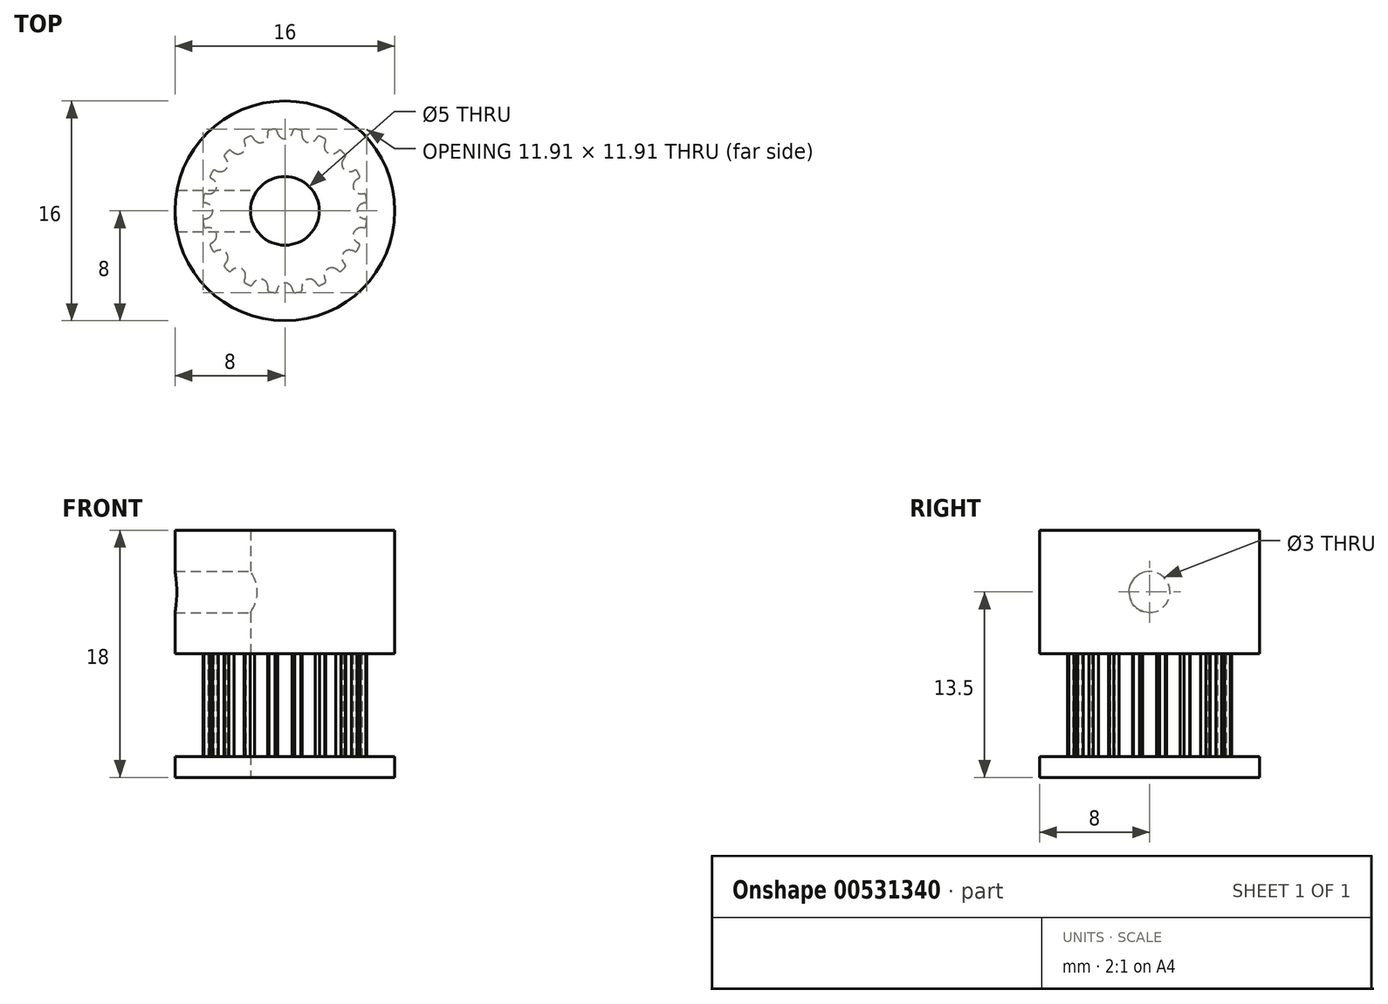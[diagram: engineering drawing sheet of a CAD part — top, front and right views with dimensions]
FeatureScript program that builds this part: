
annotation { "Feature Type Name" : "Feature", "Feature Type Description" : "" }
export const myFeature = defineFeature(function(context is Context, id is Id, definition is map)
    precondition{}
    {
        {
            var Q0;
            Q0=qCreatedBy(makeId("Top.planeOp"),FACE);
            var sketch = newSketch(context, id + "F0", { "sketchPlane" : qUnion([Q0])});
            skLineSegment(sketch, "E0", {"start": v(-19.17, 17.78) * mm, "end": v(-18.17, 17.78) * mm});
            skLineSegment(sketch, "E1", {"start": v(-18.17, 17.78) * mm, "end": v(-18.17, 18.4) * mm});
            skArc(sketch, "E2", {"start": v(-18.67, 18.85) * mm, "mid": v(-18.88, 19.07) * mm, "end": v(-19.17, 19.16) * mm});
            skArc(sketch, "E3", {"start": v(-18.58, 18.54) * mm, "mid": v(-18.61, 18.7) * mm, "end": v(-18.67, 18.85) * mm});
            skArc(sketch, "E4", {"start": v(-18.58, 18.54) * mm, "mid": v(-18.53, 18.44) * mm, "end": v(-18.43, 18.4) * mm});
            skLineSegment(sketch, "E5", {"start": v(-18.43, 18.4) * mm, "end": v(-18.17, 18.4) * mm});
            skArc(sketch, "E6.0.MirrorCS", {"start": v(-19.67, 18.85) * mm, "mid": v(-19.47, 19.07) * mm, "end": v(-19.17, 19.16) * mm});
            skArc(sketch, "E7.0.MirrorCS", {"start": v(-19.76, 18.54) * mm, "mid": v(-19.73, 18.7) * mm, "end": v(-19.67, 18.85) * mm});
            skArc(sketch, "E8.0.MirrorCS", {"start": v(-19.76, 18.54) * mm, "mid": v(-19.81, 18.44) * mm, "end": v(-19.91, 18.4) * mm});
            skLineSegment(sketch, "E9.0.MirrorCS", {"start": v(-19.91, 18.4) * mm, "end": v(-20.17, 18.4) * mm});
            skLineSegment(sketch, "E10.0.MirrorCS", {"start": v(-20.17, 17.78) * mm, "end": v(-20.17, 18.4) * mm});
            skLineSegment(sketch, "E11.0.MirrorCS", {"start": v(-19.17, 17.78) * mm, "end": v(-20.17, 17.78) * mm});
            skLineSegment(sketch, "E12.direction1", {"start": v(-20.17, 17.78) * mm, "end": v(-18.17, 17.78) * mm, "construction": true});
            skLineSegment(sketch, "E13", {"start": v(-20.17, 18.15) * mm, "end": v(-18.17, 18.15) * mm, "construction": true});
            skPoint(sketch, "E14", {"position": v(0, -5.25) * mm});
            skArc(sketch, "E15", {"start": v(0.51, -5.6) * mm, "mid": v(0, -5.25) * mm, "end": v(-0.51, -5.6) * mm});
            skArc(sketch, "E16", {"start": v(-0.51, -5.6) * mm, "mid": v(-0.56, -5.71) * mm, "end": v(-0.59, -5.83) * mm});
            skArc(sketch, "E17", {"start": v(0.59, -5.83) * mm, "mid": v(0.56, -5.71) * mm, "end": v(0.51, -5.6) * mm});
            skArc(sketch, "E18", {"start": v(0.72, -5.96) * mm, "mid": v(0.94, -5.93) * mm, "end": v(1.16, -5.89) * mm});
            skArc(sketch, "E19", {"start": v(0.59, -5.83) * mm, "mid": v(0.66, -5.94) * mm, "end": v(0.8, -5.95) * mm});
            skArc(sketch, "E20", {"start": v(-0.59, -5.83) * mm, "mid": v(-0.66, -5.94) * mm, "end": v(-0.8, -5.95) * mm});
            skArc(sketch, "E21.1.0", {"start": v(2.22, -5.16) * mm, "mid": v(1.62, -5) * mm, "end": v(1.24, -5.48) * mm});
            skPoint(sketch, "E21.1.1", {"position": v(1.62, -5) * mm});
            skArc(sketch, "E21.1.2", {"start": v(1.24, -5.48) * mm, "mid": v(1.23, -5.6) * mm, "end": v(1.24, -5.73) * mm});
            skArc(sketch, "E21.1.3", {"start": v(2.36, -5.37) * mm, "mid": v(2.47, -5.44) * mm, "end": v(2.6, -5.41) * mm});
            skArc(sketch, "E21.1.4", {"start": v(1.24, -5.73) * mm, "mid": v(1.2, -5.85) * mm, "end": v(1.08, -5.9) * mm});
            skArc(sketch, "E21.1.5", {"start": v(2.36, -5.37) * mm, "mid": v(2.3, -5.26) * mm, "end": v(2.22, -5.16) * mm});
            skArc(sketch, "E22.3.2.0", {"start": v(3.7, -4.22) * mm, "mid": v(3.09, -4.25) * mm, "end": v(2.87, -4.83) * mm});
            skPoint(sketch, "E22.4.2.0", {"position": v(3.09, -4.25) * mm});
            skArc(sketch, "E22.5.2.0", {"start": v(2.87, -4.83) * mm, "mid": v(2.9, -4.95) * mm, "end": v(2.95, -5.07) * mm});
            skArc(sketch, "E22.9.2.0", {"start": v(3.9, -4.37) * mm, "mid": v(4.03, -4.41) * mm, "end": v(4.14, -4.35) * mm});
            skArc(sketch, "E22.13.2.0", {"start": v(2.95, -5.07) * mm, "mid": v(2.95, -5.2) * mm, "end": v(2.85, -5.28) * mm});
            skArc(sketch, "E22.17.2.0", {"start": v(3.9, -4.37) * mm, "mid": v(3.81, -4.3) * mm, "end": v(3.7, -4.22) * mm});
            skArc(sketch, "E22.3.3.0", {"start": v(4.83, -2.87) * mm, "mid": v(4.25, -3.09) * mm, "end": v(4.22, -3.7) * mm});
            skPoint(sketch, "E22.4.3.0", {"position": v(4.25, -3.09) * mm});
            skArc(sketch, "E22.5.3.0", {"start": v(4.22, -3.7) * mm, "mid": v(4.3, -3.81) * mm, "end": v(4.37, -3.9) * mm});
            skArc(sketch, "E22.9.3.0", {"start": v(5.07, -2.95) * mm, "mid": v(5.2, -2.95) * mm, "end": v(5.28, -2.85) * mm});
            skArc(sketch, "E22.13.3.0", {"start": v(4.37, -3.9) * mm, "mid": v(4.41, -4.03) * mm, "end": v(4.35, -4.14) * mm});
            skArc(sketch, "E22.17.3.0", {"start": v(5.07, -2.95) * mm, "mid": v(4.95, -2.9) * mm, "end": v(4.83, -2.87) * mm});
            skArc(sketch, "E22.3.4.0", {"start": v(5.48, -1.24) * mm, "mid": v(5, -1.62) * mm, "end": v(5.16, -2.22) * mm});
            skPoint(sketch, "E22.4.4.0", {"position": v(5, -1.62) * mm});
            skArc(sketch, "E22.5.4.0", {"start": v(5.16, -2.22) * mm, "mid": v(5.26, -2.3) * mm, "end": v(5.37, -2.36) * mm});
            skArc(sketch, "E22.9.4.0", {"start": v(5.73, -1.24) * mm, "mid": v(5.85, -1.2) * mm, "end": v(5.9, -1.08) * mm});
            skArc(sketch, "E22.13.4.0", {"start": v(5.37, -2.36) * mm, "mid": v(5.44, -2.47) * mm, "end": v(5.41, -2.6) * mm});
            skArc(sketch, "E22.17.4.0", {"start": v(5.73, -1.24) * mm, "mid": v(5.6, -1.23) * mm, "end": v(5.48, -1.24) * mm});
            skArc(sketch, "E22.3.5.0", {"start": v(5.6, 0.51) * mm, "mid": v(5.25, 0) * mm, "end": v(5.6, -0.51) * mm});
            skPoint(sketch, "E22.4.5.0", {"position": v(5.25, 0) * mm});
            skArc(sketch, "E22.5.5.0", {"start": v(5.6, -0.51) * mm, "mid": v(5.71, -0.56) * mm, "end": v(5.83, -0.59) * mm});
            skArc(sketch, "E22.9.5.0", {"start": v(5.83, 0.59) * mm, "mid": v(5.94, 0.66) * mm, "end": v(5.95, 0.8) * mm});
            skArc(sketch, "E22.13.5.0", {"start": v(5.83, -0.59) * mm, "mid": v(5.94, -0.66) * mm, "end": v(5.95, -0.8) * mm});
            skArc(sketch, "E22.17.5.0", {"start": v(5.83, 0.59) * mm, "mid": v(5.71, 0.56) * mm, "end": v(5.6, 0.51) * mm});
            skArc(sketch, "E22.3.6.0", {"start": v(5.16, 2.22) * mm, "mid": v(5, 1.62) * mm, "end": v(5.48, 1.24) * mm});
            skPoint(sketch, "E22.4.6.0", {"position": v(5, 1.62) * mm});
            skArc(sketch, "E22.5.6.0", {"start": v(5.48, 1.24) * mm, "mid": v(5.6, 1.23) * mm, "end": v(5.73, 1.24) * mm});
            skArc(sketch, "E22.9.6.0", {"start": v(5.37, 2.36) * mm, "mid": v(5.44, 2.47) * mm, "end": v(5.41, 2.6) * mm});
            skArc(sketch, "E22.13.6.0", {"start": v(5.73, 1.24) * mm, "mid": v(5.85, 1.2) * mm, "end": v(5.9, 1.08) * mm});
            skArc(sketch, "E22.17.6.0", {"start": v(5.37, 2.36) * mm, "mid": v(5.26, 2.3) * mm, "end": v(5.16, 2.22) * mm});
            skArc(sketch, "E22.3.7.0", {"start": v(4.22, 3.7) * mm, "mid": v(4.25, 3.09) * mm, "end": v(4.83, 2.87) * mm});
            skPoint(sketch, "E22.4.7.0", {"position": v(4.25, 3.09) * mm});
            skArc(sketch, "E22.5.7.0", {"start": v(4.83, 2.87) * mm, "mid": v(4.95, 2.9) * mm, "end": v(5.07, 2.95) * mm});
            skArc(sketch, "E22.9.7.0", {"start": v(4.37, 3.9) * mm, "mid": v(4.41, 4.03) * mm, "end": v(4.35, 4.14) * mm});
            skArc(sketch, "E22.13.7.0", {"start": v(5.07, 2.95) * mm, "mid": v(5.2, 2.95) * mm, "end": v(5.28, 2.85) * mm});
            skArc(sketch, "E22.17.7.0", {"start": v(4.37, 3.9) * mm, "mid": v(4.3, 3.81) * mm, "end": v(4.22, 3.7) * mm});
            skArc(sketch, "E22.3.8.0", {"start": v(2.87, 4.83) * mm, "mid": v(3.09, 4.25) * mm, "end": v(3.7, 4.22) * mm});
            skPoint(sketch, "E22.4.8.0", {"position": v(3.09, 4.25) * mm});
            skArc(sketch, "E22.5.8.0", {"start": v(3.7, 4.22) * mm, "mid": v(3.81, 4.3) * mm, "end": v(3.9, 4.37) * mm});
            skArc(sketch, "E22.9.8.0", {"start": v(2.95, 5.07) * mm, "mid": v(2.95, 5.2) * mm, "end": v(2.85, 5.28) * mm});
            skArc(sketch, "E22.13.8.0", {"start": v(3.9, 4.37) * mm, "mid": v(4.03, 4.41) * mm, "end": v(4.14, 4.35) * mm});
            skArc(sketch, "E22.17.8.0", {"start": v(2.95, 5.07) * mm, "mid": v(2.9, 4.95) * mm, "end": v(2.87, 4.83) * mm});
            skArc(sketch, "E22.3.9.0", {"start": v(1.24, 5.48) * mm, "mid": v(1.62, 5) * mm, "end": v(2.22, 5.16) * mm});
            skPoint(sketch, "E22.4.9.0", {"position": v(1.62, 5) * mm});
            skArc(sketch, "E22.5.9.0", {"start": v(2.22, 5.16) * mm, "mid": v(2.3, 5.26) * mm, "end": v(2.36, 5.37) * mm});
            skArc(sketch, "E22.9.9.0", {"start": v(1.24, 5.73) * mm, "mid": v(1.2, 5.85) * mm, "end": v(1.08, 5.9) * mm});
            skArc(sketch, "E22.13.9.0", {"start": v(2.36, 5.37) * mm, "mid": v(2.47, 5.44) * mm, "end": v(2.6, 5.41) * mm});
            skArc(sketch, "E22.17.9.0", {"start": v(1.24, 5.73) * mm, "mid": v(1.23, 5.6) * mm, "end": v(1.24, 5.48) * mm});
            skArc(sketch, "E22.3.10.0", {"start": v(-0.51, 5.6) * mm, "mid": v(0, 5.25) * mm, "end": v(0.51, 5.6) * mm});
            skPoint(sketch, "E22.4.10.0", {"position": v(0, 5.25) * mm});
            skArc(sketch, "E22.5.10.0", {"start": v(0.51, 5.6) * mm, "mid": v(0.56, 5.71) * mm, "end": v(0.59, 5.83) * mm});
            skArc(sketch, "E22.9.10.0", {"start": v(-0.59, 5.83) * mm, "mid": v(-0.66, 5.94) * mm, "end": v(-0.8, 5.95) * mm});
            skArc(sketch, "E22.13.10.0", {"start": v(0.59, 5.83) * mm, "mid": v(0.66, 5.94) * mm, "end": v(0.8, 5.95) * mm});
            skArc(sketch, "E22.17.10.0", {"start": v(-0.59, 5.83) * mm, "mid": v(-0.56, 5.71) * mm, "end": v(-0.51, 5.6) * mm});
            skArc(sketch, "E22.3.11.0", {"start": v(-2.22, 5.16) * mm, "mid": v(-1.62, 5) * mm, "end": v(-1.24, 5.48) * mm});
            skPoint(sketch, "E22.4.11.0", {"position": v(-1.62, 5) * mm});
            skArc(sketch, "E22.5.11.0", {"start": v(-1.24, 5.48) * mm, "mid": v(-1.23, 5.6) * mm, "end": v(-1.24, 5.73) * mm});
            skArc(sketch, "E22.9.11.0", {"start": v(-2.36, 5.37) * mm, "mid": v(-2.47, 5.44) * mm, "end": v(-2.6, 5.41) * mm});
            skArc(sketch, "E22.13.11.0", {"start": v(-1.24, 5.73) * mm, "mid": v(-1.2, 5.85) * mm, "end": v(-1.08, 5.9) * mm});
            skArc(sketch, "E22.17.11.0", {"start": v(-2.36, 5.37) * mm, "mid": v(-2.3, 5.26) * mm, "end": v(-2.22, 5.16) * mm});
            skArc(sketch, "E22.3.12.0", {"start": v(-3.7, 4.22) * mm, "mid": v(-3.09, 4.25) * mm, "end": v(-2.87, 4.83) * mm});
            skPoint(sketch, "E22.4.12.0", {"position": v(-3.09, 4.25) * mm});
            skArc(sketch, "E22.5.12.0", {"start": v(-2.87, 4.83) * mm, "mid": v(-2.9, 4.95) * mm, "end": v(-2.95, 5.07) * mm});
            skArc(sketch, "E22.9.12.0", {"start": v(-3.9, 4.37) * mm, "mid": v(-4.03, 4.41) * mm, "end": v(-4.14, 4.35) * mm});
            skArc(sketch, "E22.13.12.0", {"start": v(-2.95, 5.07) * mm, "mid": v(-2.95, 5.2) * mm, "end": v(-2.85, 5.28) * mm});
            skArc(sketch, "E22.17.12.0", {"start": v(-3.9, 4.37) * mm, "mid": v(-3.81, 4.3) * mm, "end": v(-3.7, 4.22) * mm});
            skArc(sketch, "E22.3.13.0", {"start": v(-4.83, 2.87) * mm, "mid": v(-4.25, 3.09) * mm, "end": v(-4.22, 3.7) * mm});
            skPoint(sketch, "E22.4.13.0", {"position": v(-4.25, 3.09) * mm});
            skArc(sketch, "E22.5.13.0", {"start": v(-4.22, 3.7) * mm, "mid": v(-4.3, 3.81) * mm, "end": v(-4.37, 3.9) * mm});
            skArc(sketch, "E22.9.13.0", {"start": v(-5.07, 2.95) * mm, "mid": v(-5.2, 2.95) * mm, "end": v(-5.28, 2.85) * mm});
            skArc(sketch, "E22.13.13.0", {"start": v(-4.37, 3.9) * mm, "mid": v(-4.41, 4.03) * mm, "end": v(-4.35, 4.14) * mm});
            skArc(sketch, "E22.17.13.0", {"start": v(-5.07, 2.95) * mm, "mid": v(-4.95, 2.9) * mm, "end": v(-4.83, 2.87) * mm});
            skArc(sketch, "E22.3.14.0", {"start": v(-5.48, 1.24) * mm, "mid": v(-5, 1.62) * mm, "end": v(-5.16, 2.22) * mm});
            skPoint(sketch, "E22.4.14.0", {"position": v(-5, 1.62) * mm});
            skArc(sketch, "E22.5.14.0", {"start": v(-5.16, 2.22) * mm, "mid": v(-5.26, 2.3) * mm, "end": v(-5.37, 2.36) * mm});
            skArc(sketch, "E22.9.14.0", {"start": v(-5.73, 1.24) * mm, "mid": v(-5.85, 1.2) * mm, "end": v(-5.9, 1.08) * mm});
            skArc(sketch, "E22.13.14.0", {"start": v(-5.37, 2.36) * mm, "mid": v(-5.44, 2.47) * mm, "end": v(-5.41, 2.6) * mm});
            skArc(sketch, "E22.17.14.0", {"start": v(-5.73, 1.24) * mm, "mid": v(-5.6, 1.23) * mm, "end": v(-5.48, 1.24) * mm});
            skArc(sketch, "E22.3.15.0", {"start": v(-5.6, -0.51) * mm, "mid": v(-5.25, 0) * mm, "end": v(-5.6, 0.51) * mm});
            skPoint(sketch, "E22.4.15.0", {"position": v(-5.25, 0) * mm});
            skArc(sketch, "E22.5.15.0", {"start": v(-5.6, 0.51) * mm, "mid": v(-5.71, 0.56) * mm, "end": v(-5.83, 0.59) * mm});
            skArc(sketch, "E22.9.15.0", {"start": v(-5.83, -0.59) * mm, "mid": v(-5.94, -0.66) * mm, "end": v(-5.95, -0.8) * mm});
            skArc(sketch, "E22.13.15.0", {"start": v(-5.83, 0.59) * mm, "mid": v(-5.94, 0.66) * mm, "end": v(-5.95, 0.8) * mm});
            skArc(sketch, "E22.17.15.0", {"start": v(-5.83, -0.59) * mm, "mid": v(-5.71, -0.56) * mm, "end": v(-5.6, -0.51) * mm});
            skArc(sketch, "E22.3.16.0", {"start": v(-5.16, -2.22) * mm, "mid": v(-5, -1.62) * mm, "end": v(-5.48, -1.24) * mm});
            skPoint(sketch, "E22.4.16.0", {"position": v(-5, -1.62) * mm});
            skArc(sketch, "E22.5.16.0", {"start": v(-5.48, -1.24) * mm, "mid": v(-5.6, -1.23) * mm, "end": v(-5.73, -1.24) * mm});
            skArc(sketch, "E22.9.16.0", {"start": v(-5.37, -2.36) * mm, "mid": v(-5.44, -2.47) * mm, "end": v(-5.41, -2.6) * mm});
            skArc(sketch, "E22.13.16.0", {"start": v(-5.73, -1.24) * mm, "mid": v(-5.85, -1.2) * mm, "end": v(-5.9, -1.08) * mm});
            skArc(sketch, "E22.17.16.0", {"start": v(-5.37, -2.36) * mm, "mid": v(-5.26, -2.3) * mm, "end": v(-5.16, -2.22) * mm});
            skArc(sketch, "E22.3.17.0", {"start": v(-4.22, -3.7) * mm, "mid": v(-4.25, -3.09) * mm, "end": v(-4.83, -2.87) * mm});
            skPoint(sketch, "E22.4.17.0", {"position": v(-4.25, -3.09) * mm});
            skArc(sketch, "E22.5.17.0", {"start": v(-4.83, -2.87) * mm, "mid": v(-4.95, -2.9) * mm, "end": v(-5.07, -2.95) * mm});
            skArc(sketch, "E22.9.17.0", {"start": v(-4.37, -3.9) * mm, "mid": v(-4.41, -4.03) * mm, "end": v(-4.35, -4.14) * mm});
            skArc(sketch, "E22.13.17.0", {"start": v(-5.07, -2.95) * mm, "mid": v(-5.2, -2.95) * mm, "end": v(-5.28, -2.85) * mm});
            skArc(sketch, "E22.17.17.0", {"start": v(-4.37, -3.9) * mm, "mid": v(-4.3, -3.81) * mm, "end": v(-4.22, -3.7) * mm});
            skArc(sketch, "E22.3.18.0", {"start": v(-2.87, -4.83) * mm, "mid": v(-3.09, -4.25) * mm, "end": v(-3.7, -4.22) * mm});
            skPoint(sketch, "E22.4.18.0", {"position": v(-3.09, -4.25) * mm});
            skArc(sketch, "E22.5.18.0", {"start": v(-3.7, -4.22) * mm, "mid": v(-3.81, -4.3) * mm, "end": v(-3.9, -4.37) * mm});
            skArc(sketch, "E22.9.18.0", {"start": v(-2.95, -5.07) * mm, "mid": v(-2.95, -5.2) * mm, "end": v(-2.85, -5.28) * mm});
            skArc(sketch, "E22.13.18.0", {"start": v(-3.9, -4.37) * mm, "mid": v(-4.03, -4.41) * mm, "end": v(-4.14, -4.35) * mm});
            skArc(sketch, "E22.17.18.0", {"start": v(-2.95, -5.07) * mm, "mid": v(-2.9, -4.95) * mm, "end": v(-2.87, -4.83) * mm});
            skArc(sketch, "E22.3.19.0", {"start": v(-1.24, -5.48) * mm, "mid": v(-1.62, -5) * mm, "end": v(-2.22, -5.16) * mm});
            skPoint(sketch, "E22.4.19.0", {"position": v(-1.62, -5) * mm});
            skArc(sketch, "E22.5.19.0", {"start": v(-2.22, -5.16) * mm, "mid": v(-2.3, -5.26) * mm, "end": v(-2.36, -5.37) * mm});
            skArc(sketch, "E22.9.19.0", {"start": v(-1.24, -5.73) * mm, "mid": v(-1.2, -5.85) * mm, "end": v(-1.08, -5.9) * mm});
            skArc(sketch, "E22.13.19.0", {"start": v(-2.36, -5.37) * mm, "mid": v(-2.47, -5.44) * mm, "end": v(-2.6, -5.41) * mm});
            skArc(sketch, "E22.17.19.0", {"start": v(-1.24, -5.73) * mm, "mid": v(-1.23, -5.6) * mm, "end": v(-1.24, -5.48) * mm});
            skArc(sketch, "E23.trimOffspring", {"start": v(2.52, -5.44) * mm, "mid": v(2.72, -5.35) * mm, "end": v(2.92, -5.24) * mm});
            skArc(sketch, "E24.trimOffspring", {"start": v(4.08, -4.4) * mm, "mid": v(4.24, -4.24) * mm, "end": v(4.4, -4.08) * mm});
            skArc(sketch, "E25.trimOffspring", {"start": v(5.24, -2.92) * mm, "mid": v(5.33, -2.76) * mm, "end": v(5.41, -2.6) * mm});
            skArc(sketch, "E26.trimOffspring", {"start": v(5.89, -1.16) * mm, "mid": v(5.93, -0.94) * mm, "end": v(5.96, -0.72) * mm});
            skArc(sketch, "E27.trimOffspring", {"start": v(5.44, 2.52) * mm, "mid": v(5.35, 2.72) * mm, "end": v(5.24, 2.92) * mm});
            skArc(sketch, "E28.trimOffspring", {"start": v(4.4, 4.08) * mm, "mid": v(4.24, 4.24) * mm, "end": v(4.08, 4.4) * mm});
            skArc(sketch, "E29.trimOffspring", {"start": v(5.96, 0.72) * mm, "mid": v(5.93, 0.94) * mm, "end": v(5.89, 1.16) * mm});
            skArc(sketch, "E30.trimOffspring", {"start": v(2.92, 5.24) * mm, "mid": v(2.72, 5.35) * mm, "end": v(2.52, 5.44) * mm});
            skArc(sketch, "E31.trimOffspring", {"start": v(1.16, 5.89) * mm, "mid": v(0.94, 5.93) * mm, "end": v(0.72, 5.96) * mm});
            skArc(sketch, "E32.trimOffspring", {"start": v(-0.72, 5.96) * mm, "mid": v(-0.94, 5.93) * mm, "end": v(-1.16, 5.89) * mm});
            skArc(sketch, "E33.trimOffspring", {"start": v(-2.52, 5.44) * mm, "mid": v(-2.72, 5.35) * mm, "end": v(-2.92, 5.24) * mm});
            skArc(sketch, "E34.trimOffspring", {"start": v(-4.08, 4.4) * mm, "mid": v(-4.24, 4.24) * mm, "end": v(-4.4, 4.08) * mm});
            skArc(sketch, "E35.trimOffspring", {"start": v(-5.24, 2.92) * mm, "mid": v(-5.35, 2.72) * mm, "end": v(-5.44, 2.52) * mm});
            skArc(sketch, "E36.trimOffspring", {"start": v(-5.89, 1.16) * mm, "mid": v(-5.93, 0.94) * mm, "end": v(-5.96, 0.72) * mm});
            skArc(sketch, "E37.trimOffspring", {"start": v(-5.96, -0.72) * mm, "mid": v(-5.93, -0.94) * mm, "end": v(-5.89, -1.16) * mm});
            skArc(sketch, "E38.trimOffspring", {"start": v(-5.44, -2.52) * mm, "mid": v(-5.35, -2.72) * mm, "end": v(-5.24, -2.92) * mm});
            skArc(sketch, "E39.trimOffspring", {"start": v(-4.4, -4.08) * mm, "mid": v(-4.24, -4.24) * mm, "end": v(-4.08, -4.4) * mm});
            skArc(sketch, "E40.trimOffspring", {"start": v(-2.92, -5.24) * mm, "mid": v(-2.72, -5.35) * mm, "end": v(-2.52, -5.44) * mm});
            skArc(sketch, "E41.trimOffspring", {"start": v(-1.16, -5.89) * mm, "mid": v(-0.94, -5.93) * mm, "end": v(-0.72, -5.96) * mm});
            skSolve(sketch);
        }
        {
            var Q0;
            Q0=makeQuery(id+"F0.imprint","IMPRINT",FACE,{"disambiguationData":[TD([[makeQuery(id+"F0.imprint","IMPRINT",EDGE,{"derivedFrom":sQuery(id+"F0.wireOp",EDGE,"E15")}),-1.0]])]});
            extrude(context, id + "F1", {"entities" : qUnion([Q0]), "depth" : 7.5 * mm, "offsetDistance" : 25 * mm});
        }
        {
            var Q0;
            Q0=makeQuery(id+"F1.opExtrude","CAP_FACE",FACE,{"disambiguationData":[OSD([sQuery(id+"F0.wireOp",EDGE,"E15"),sQuery(id+"F0.wireOp",EDGE,"E16"),sQuery(id+"F0.wireOp",EDGE,"E17"),sQuery(id+"F0.wireOp",EDGE,"E18"),sQuery(id+"F0.wireOp",EDGE,"E19"),sQuery(id+"F0.wireOp",EDGE,"E20"),sQuery(id+"F0.wireOp",EDGE,"E21.1.0"),sQuery(id+"F0.wireOp",EDGE,"E21.1.2"),sQuery(id+"F0.wireOp",EDGE,"E21.1.3"),sQuery(id+"F0.wireOp",EDGE,"E21.1.4"),sQuery(id+"F0.wireOp",EDGE,"E21.1.5"),sQuery(id+"F0.wireOp",EDGE,"E22.3.2.0"),sQuery(id+"F0.wireOp",EDGE,"E22.5.2.0"),sQuery(id+"F0.wireOp",EDGE,"E22.9.2.0"),sQuery(id+"F0.wireOp",EDGE,"E22.13.2.0"),sQuery(id+"F0.wireOp",EDGE,"E22.17.2.0"),sQuery(id+"F0.wireOp",EDGE,"E22.3.3.0"),sQuery(id+"F0.wireOp",EDGE,"E22.5.3.0"),sQuery(id+"F0.wireOp",EDGE,"E22.9.3.0"),sQuery(id+"F0.wireOp",EDGE,"E22.13.3.0"),sQuery(id+"F0.wireOp",EDGE,"E22.17.3.0"),sQuery(id+"F0.wireOp",EDGE,"E22.3.4.0"),sQuery(id+"F0.wireOp",EDGE,"E22.5.4.0"),sQuery(id+"F0.wireOp",EDGE,"E22.9.4.0"),sQuery(id+"F0.wireOp",EDGE,"E22.13.4.0"),sQuery(id+"F0.wireOp",EDGE,"E22.17.4.0"),sQuery(id+"F0.wireOp",EDGE,"E22.3.5.0"),sQuery(id+"F0.wireOp",EDGE,"E22.5.5.0"),sQuery(id+"F0.wireOp",EDGE,"E22.9.5.0"),sQuery(id+"F0.wireOp",EDGE,"E22.13.5.0"),sQuery(id+"F0.wireOp",EDGE,"E22.17.5.0"),sQuery(id+"F0.wireOp",EDGE,"E22.3.6.0"),sQuery(id+"F0.wireOp",EDGE,"E22.5.6.0"),sQuery(id+"F0.wireOp",EDGE,"E22.9.6.0"),sQuery(id+"F0.wireOp",EDGE,"E22.13.6.0"),sQuery(id+"F0.wireOp",EDGE,"E22.17.6.0"),sQuery(id+"F0.wireOp",EDGE,"E22.3.7.0"),sQuery(id+"F0.wireOp",EDGE,"E22.5.7.0"),sQuery(id+"F0.wireOp",EDGE,"E22.9.7.0"),sQuery(id+"F0.wireOp",EDGE,"E22.13.7.0"),sQuery(id+"F0.wireOp",EDGE,"E22.17.7.0"),sQuery(id+"F0.wireOp",EDGE,"E22.3.8.0"),sQuery(id+"F0.wireOp",EDGE,"E22.5.8.0"),sQuery(id+"F0.wireOp",EDGE,"E22.9.8.0"),sQuery(id+"F0.wireOp",EDGE,"E22.13.8.0"),sQuery(id+"F0.wireOp",EDGE,"E22.17.8.0"),sQuery(id+"F0.wireOp",EDGE,"E22.3.9.0"),sQuery(id+"F0.wireOp",EDGE,"E22.5.9.0"),sQuery(id+"F0.wireOp",EDGE,"E22.9.9.0"),sQuery(id+"F0.wireOp",EDGE,"E22.13.9.0"),sQuery(id+"F0.wireOp",EDGE,"E22.17.9.0"),sQuery(id+"F0.wireOp",EDGE,"E22.3.10.0"),sQuery(id+"F0.wireOp",EDGE,"E22.5.10.0"),sQuery(id+"F0.wireOp",EDGE,"E22.9.10.0"),sQuery(id+"F0.wireOp",EDGE,"E22.13.10.0"),sQuery(id+"F0.wireOp",EDGE,"E22.17.10.0"),sQuery(id+"F0.wireOp",EDGE,"E22.3.11.0"),sQuery(id+"F0.wireOp",EDGE,"E22.5.11.0"),sQuery(id+"F0.wireOp",EDGE,"E22.9.11.0"),sQuery(id+"F0.wireOp",EDGE,"E22.13.11.0"),sQuery(id+"F0.wireOp",EDGE,"E22.17.11.0"),sQuery(id+"F0.wireOp",EDGE,"E22.3.12.0"),sQuery(id+"F0.wireOp",EDGE,"E22.5.12.0"),sQuery(id+"F0.wireOp",EDGE,"E22.9.12.0"),sQuery(id+"F0.wireOp",EDGE,"E22.13.12.0"),sQuery(id+"F0.wireOp",EDGE,"E22.17.12.0"),sQuery(id+"F0.wireOp",EDGE,"E22.3.13.0"),sQuery(id+"F0.wireOp",EDGE,"E22.5.13.0"),sQuery(id+"F0.wireOp",EDGE,"E22.9.13.0"),sQuery(id+"F0.wireOp",EDGE,"E22.13.13.0"),sQuery(id+"F0.wireOp",EDGE,"E22.17.13.0"),sQuery(id+"F0.wireOp",EDGE,"E22.3.14.0"),sQuery(id+"F0.wireOp",EDGE,"E22.5.14.0"),sQuery(id+"F0.wireOp",EDGE,"E22.9.14.0"),sQuery(id+"F0.wireOp",EDGE,"E22.13.14.0"),sQuery(id+"F0.wireOp",EDGE,"E22.17.14.0"),sQuery(id+"F0.wireOp",EDGE,"E22.3.15.0"),sQuery(id+"F0.wireOp",EDGE,"E22.5.15.0"),sQuery(id+"F0.wireOp",EDGE,"E22.9.15.0"),sQuery(id+"F0.wireOp",EDGE,"E22.13.15.0"),sQuery(id+"F0.wireOp",EDGE,"E22.17.15.0"),sQuery(id+"F0.wireOp",EDGE,"E22.3.16.0"),sQuery(id+"F0.wireOp",EDGE,"E22.5.16.0"),sQuery(id+"F0.wireOp",EDGE,"E22.9.16.0"),sQuery(id+"F0.wireOp",EDGE,"E22.13.16.0"),sQuery(id+"F0.wireOp",EDGE,"E22.17.16.0"),sQuery(id+"F0.wireOp",EDGE,"E22.3.17.0"),sQuery(id+"F0.wireOp",EDGE,"E22.5.17.0"),sQuery(id+"F0.wireOp",EDGE,"E22.9.17.0"),sQuery(id+"F0.wireOp",EDGE,"E22.13.17.0"),sQuery(id+"F0.wireOp",EDGE,"E22.17.17.0"),sQuery(id+"F0.wireOp",EDGE,"E22.3.18.0"),sQuery(id+"F0.wireOp",EDGE,"E22.5.18.0"),sQuery(id+"F0.wireOp",EDGE,"E22.9.18.0"),sQuery(id+"F0.wireOp",EDGE,"E22.13.18.0"),sQuery(id+"F0.wireOp",EDGE,"E22.17.18.0"),sQuery(id+"F0.wireOp",EDGE,"E22.3.19.0"),sQuery(id+"F0.wireOp",EDGE,"E22.5.19.0"),sQuery(id+"F0.wireOp",EDGE,"E22.9.19.0"),sQuery(id+"F0.wireOp",EDGE,"E22.13.19.0"),sQuery(id+"F0.wireOp",EDGE,"E22.17.19.0"),sQuery(id+"F0.wireOp",EDGE,"E23.trimOffspring"),sQuery(id+"F0.wireOp",EDGE,"E24.trimOffspring"),sQuery(id+"F0.wireOp",EDGE,"E25.trimOffspring"),sQuery(id+"F0.wireOp",EDGE,"E26.trimOffspring"),sQuery(id+"F0.wireOp",EDGE,"E27.trimOffspring"),sQuery(id+"F0.wireOp",EDGE,"E28.trimOffspring"),sQuery(id+"F0.wireOp",EDGE,"E29.trimOffspring"),sQuery(id+"F0.wireOp",EDGE,"E30.trimOffspring"),sQuery(id+"F0.wireOp",EDGE,"E31.trimOffspring"),sQuery(id+"F0.wireOp",EDGE,"E32.trimOffspring"),sQuery(id+"F0.wireOp",EDGE,"E33.trimOffspring"),sQuery(id+"F0.wireOp",EDGE,"E34.trimOffspring"),sQuery(id+"F0.wireOp",EDGE,"E35.trimOffspring"),sQuery(id+"F0.wireOp",EDGE,"E36.trimOffspring"),sQuery(id+"F0.wireOp",EDGE,"E37.trimOffspring"),sQuery(id+"F0.wireOp",EDGE,"E38.trimOffspring"),sQuery(id+"F0.wireOp",EDGE,"E39.trimOffspring"),sQuery(id+"F0.wireOp",EDGE,"E40.trimOffspring"),sQuery(id+"F0.wireOp",EDGE,"E41.trimOffspring")])],"isStart":false});
            var sketch = newSketch(context, id + "F2", { "sketchPlane" : qUnion([Q0])});
            skCircle(sketch, "E42", {"center": v(0, 0) * mm, "radius": 8 * mm});
            skSolve(sketch);
        }
        {
            var Q0;
            Q0=qSketchRegion(id+"F2",true);
            extrude(context, id + "F3", {"entities" : qUnion([Q0]), "operationType" : NewBodyOperationType.ADD, "depth" : 9 * mm});
        }
        {
            var Q0;
            Q0=makeQuery(id+"F1.opExtrude","CAP_FACE",FACE,{"disambiguationData":[OSD([sQuery(id+"F0.wireOp",EDGE,"E15"),sQuery(id+"F0.wireOp",EDGE,"E16"),sQuery(id+"F0.wireOp",EDGE,"E17"),sQuery(id+"F0.wireOp",EDGE,"E18"),sQuery(id+"F0.wireOp",EDGE,"E19"),sQuery(id+"F0.wireOp",EDGE,"E20"),sQuery(id+"F0.wireOp",EDGE,"E21.1.0"),sQuery(id+"F0.wireOp",EDGE,"E21.1.2"),sQuery(id+"F0.wireOp",EDGE,"E21.1.3"),sQuery(id+"F0.wireOp",EDGE,"E21.1.4"),sQuery(id+"F0.wireOp",EDGE,"E21.1.5"),sQuery(id+"F0.wireOp",EDGE,"E22.3.2.0"),sQuery(id+"F0.wireOp",EDGE,"E22.5.2.0"),sQuery(id+"F0.wireOp",EDGE,"E22.9.2.0"),sQuery(id+"F0.wireOp",EDGE,"E22.13.2.0"),sQuery(id+"F0.wireOp",EDGE,"E22.17.2.0"),sQuery(id+"F0.wireOp",EDGE,"E22.3.3.0"),sQuery(id+"F0.wireOp",EDGE,"E22.5.3.0"),sQuery(id+"F0.wireOp",EDGE,"E22.9.3.0"),sQuery(id+"F0.wireOp",EDGE,"E22.13.3.0"),sQuery(id+"F0.wireOp",EDGE,"E22.17.3.0"),sQuery(id+"F0.wireOp",EDGE,"E22.3.4.0"),sQuery(id+"F0.wireOp",EDGE,"E22.5.4.0"),sQuery(id+"F0.wireOp",EDGE,"E22.9.4.0"),sQuery(id+"F0.wireOp",EDGE,"E22.13.4.0"),sQuery(id+"F0.wireOp",EDGE,"E22.17.4.0"),sQuery(id+"F0.wireOp",EDGE,"E22.3.5.0"),sQuery(id+"F0.wireOp",EDGE,"E22.5.5.0"),sQuery(id+"F0.wireOp",EDGE,"E22.9.5.0"),sQuery(id+"F0.wireOp",EDGE,"E22.13.5.0"),sQuery(id+"F0.wireOp",EDGE,"E22.17.5.0"),sQuery(id+"F0.wireOp",EDGE,"E22.3.6.0"),sQuery(id+"F0.wireOp",EDGE,"E22.5.6.0"),sQuery(id+"F0.wireOp",EDGE,"E22.9.6.0"),sQuery(id+"F0.wireOp",EDGE,"E22.13.6.0"),sQuery(id+"F0.wireOp",EDGE,"E22.17.6.0"),sQuery(id+"F0.wireOp",EDGE,"E22.3.7.0"),sQuery(id+"F0.wireOp",EDGE,"E22.5.7.0"),sQuery(id+"F0.wireOp",EDGE,"E22.9.7.0"),sQuery(id+"F0.wireOp",EDGE,"E22.13.7.0"),sQuery(id+"F0.wireOp",EDGE,"E22.17.7.0"),sQuery(id+"F0.wireOp",EDGE,"E22.3.8.0"),sQuery(id+"F0.wireOp",EDGE,"E22.5.8.0"),sQuery(id+"F0.wireOp",EDGE,"E22.9.8.0"),sQuery(id+"F0.wireOp",EDGE,"E22.13.8.0"),sQuery(id+"F0.wireOp",EDGE,"E22.17.8.0"),sQuery(id+"F0.wireOp",EDGE,"E22.3.9.0"),sQuery(id+"F0.wireOp",EDGE,"E22.5.9.0"),sQuery(id+"F0.wireOp",EDGE,"E22.9.9.0"),sQuery(id+"F0.wireOp",EDGE,"E22.13.9.0"),sQuery(id+"F0.wireOp",EDGE,"E22.17.9.0"),sQuery(id+"F0.wireOp",EDGE,"E22.3.10.0"),sQuery(id+"F0.wireOp",EDGE,"E22.5.10.0"),sQuery(id+"F0.wireOp",EDGE,"E22.9.10.0"),sQuery(id+"F0.wireOp",EDGE,"E22.13.10.0"),sQuery(id+"F0.wireOp",EDGE,"E22.17.10.0"),sQuery(id+"F0.wireOp",EDGE,"E22.3.11.0"),sQuery(id+"F0.wireOp",EDGE,"E22.5.11.0"),sQuery(id+"F0.wireOp",EDGE,"E22.9.11.0"),sQuery(id+"F0.wireOp",EDGE,"E22.13.11.0"),sQuery(id+"F0.wireOp",EDGE,"E22.17.11.0"),sQuery(id+"F0.wireOp",EDGE,"E22.3.12.0"),sQuery(id+"F0.wireOp",EDGE,"E22.5.12.0"),sQuery(id+"F0.wireOp",EDGE,"E22.9.12.0"),sQuery(id+"F0.wireOp",EDGE,"E22.13.12.0"),sQuery(id+"F0.wireOp",EDGE,"E22.17.12.0"),sQuery(id+"F0.wireOp",EDGE,"E22.3.13.0"),sQuery(id+"F0.wireOp",EDGE,"E22.5.13.0"),sQuery(id+"F0.wireOp",EDGE,"E22.9.13.0"),sQuery(id+"F0.wireOp",EDGE,"E22.13.13.0"),sQuery(id+"F0.wireOp",EDGE,"E22.17.13.0"),sQuery(id+"F0.wireOp",EDGE,"E22.3.14.0"),sQuery(id+"F0.wireOp",EDGE,"E22.5.14.0"),sQuery(id+"F0.wireOp",EDGE,"E22.9.14.0"),sQuery(id+"F0.wireOp",EDGE,"E22.13.14.0"),sQuery(id+"F0.wireOp",EDGE,"E22.17.14.0"),sQuery(id+"F0.wireOp",EDGE,"E22.3.15.0"),sQuery(id+"F0.wireOp",EDGE,"E22.5.15.0"),sQuery(id+"F0.wireOp",EDGE,"E22.9.15.0"),sQuery(id+"F0.wireOp",EDGE,"E22.13.15.0"),sQuery(id+"F0.wireOp",EDGE,"E22.17.15.0"),sQuery(id+"F0.wireOp",EDGE,"E22.3.16.0"),sQuery(id+"F0.wireOp",EDGE,"E22.5.16.0"),sQuery(id+"F0.wireOp",EDGE,"E22.9.16.0"),sQuery(id+"F0.wireOp",EDGE,"E22.13.16.0"),sQuery(id+"F0.wireOp",EDGE,"E22.17.16.0"),sQuery(id+"F0.wireOp",EDGE,"E22.3.17.0"),sQuery(id+"F0.wireOp",EDGE,"E22.5.17.0"),sQuery(id+"F0.wireOp",EDGE,"E22.9.17.0"),sQuery(id+"F0.wireOp",EDGE,"E22.13.17.0"),sQuery(id+"F0.wireOp",EDGE,"E22.17.17.0"),sQuery(id+"F0.wireOp",EDGE,"E22.3.18.0"),sQuery(id+"F0.wireOp",EDGE,"E22.5.18.0"),sQuery(id+"F0.wireOp",EDGE,"E22.9.18.0"),sQuery(id+"F0.wireOp",EDGE,"E22.13.18.0"),sQuery(id+"F0.wireOp",EDGE,"E22.17.18.0"),sQuery(id+"F0.wireOp",EDGE,"E22.3.19.0"),sQuery(id+"F0.wireOp",EDGE,"E22.5.19.0"),sQuery(id+"F0.wireOp",EDGE,"E22.9.19.0"),sQuery(id+"F0.wireOp",EDGE,"E22.13.19.0"),sQuery(id+"F0.wireOp",EDGE,"E22.17.19.0"),sQuery(id+"F0.wireOp",EDGE,"E23.trimOffspring"),sQuery(id+"F0.wireOp",EDGE,"E24.trimOffspring"),sQuery(id+"F0.wireOp",EDGE,"E25.trimOffspring"),sQuery(id+"F0.wireOp",EDGE,"E26.trimOffspring"),sQuery(id+"F0.wireOp",EDGE,"E27.trimOffspring"),sQuery(id+"F0.wireOp",EDGE,"E28.trimOffspring"),sQuery(id+"F0.wireOp",EDGE,"E29.trimOffspring"),sQuery(id+"F0.wireOp",EDGE,"E30.trimOffspring"),sQuery(id+"F0.wireOp",EDGE,"E31.trimOffspring"),sQuery(id+"F0.wireOp",EDGE,"E32.trimOffspring"),sQuery(id+"F0.wireOp",EDGE,"E33.trimOffspring"),sQuery(id+"F0.wireOp",EDGE,"E34.trimOffspring"),sQuery(id+"F0.wireOp",EDGE,"E35.trimOffspring"),sQuery(id+"F0.wireOp",EDGE,"E36.trimOffspring"),sQuery(id+"F0.wireOp",EDGE,"E37.trimOffspring"),sQuery(id+"F0.wireOp",EDGE,"E38.trimOffspring"),sQuery(id+"F0.wireOp",EDGE,"E39.trimOffspring"),sQuery(id+"F0.wireOp",EDGE,"E40.trimOffspring"),sQuery(id+"F0.wireOp",EDGE,"E41.trimOffspring")])],"isStart":true});
            var sketch = newSketch(context, id + "F4", { "sketchPlane" : qUnion([Q0])});
            skCircle(sketch, "E43", {"center": v(0, 0) * mm, "radius": 8 * mm});
            skSolve(sketch);
        }
        {
            var Q0;
            Q0=qSketchRegion(id+"F4",true);
            extrude(context, id + "F5", {"entities" : qUnion([Q0]), "operationType" : NewBodyOperationType.ADD, "depth" : 1.5 * mm});
        }
        {
            var Q0;
            Q0=makeQuery(id+"F5.opExtrude","CAP_FACE",FACE,{"disambiguationData":[OSD([sQuery(id+"F4.wireOp",EDGE,"E43")])],"isStart":false});
            var sketch = newSketch(context, id + "F6", { "sketchPlane" : qUnion([Q0])});
            skCircle(sketch, "E44", {"center": v(0, 0) * mm, "radius": 2.5 * mm});
            skSolve(sketch);
        }
        {
            var Q0;
            Q0=qSketchRegion(id+"F6",true);
            extrude(context, id + "F7", {"entities" : qUnion([Q0]), "operationType" : NewBodyOperationType.REMOVE, "endBound" : BoundingType.THROUGH_ALL, "oppositeDirection" : true, "depth" : 25 * mm});
        }
        {
            var Q0;
            Q0=qCreatedBy(makeId("Right.planeOp"),FACE);
            var sketch = newSketch(context, id + "F8", { "sketchPlane" : qUnion([Q0])});
            skCircle(sketch, "E45", {"center": v(0, 12) * mm, "radius": 1.5 * mm});
            skSolve(sketch);
        }
        {
            var Q0;
            Q0=qSketchRegion(id+"F8",true);
            extrude(context, id + "F9", {"entities" : qUnion([Q0]), "operationType" : NewBodyOperationType.REMOVE, "endBound" : BoundingType.THROUGH_ALL, "oppositeDirection" : true, "depth" : 25 * mm});
        }
    });
